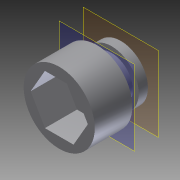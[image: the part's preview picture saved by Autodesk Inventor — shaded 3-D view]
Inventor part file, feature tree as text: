
AUTODESK INVENTOR PART (.ipt)
format: ipt  version: 2012 (Build 160160000, 160)  size: 111,104 bytes
history: native  units: in
note: dims shown in document units (in); Inventor stores cm internally (conversion verified against a paired STEP export)
features: extrude x4, sketch x4, plane x2
ambient origin geometry x8: Origin, YZ Plane, XZ Plane, XY Plane, X Axis, Y Axis, Z Axis, Center Point
bodies: Solid1 (feature_tree)
feature tree (10):
  plane  "Work Plane3"
  plane  "Work Plane4"
  extrude  "Extrusion5"  Depth=0.6264in
  extrude  "Extrusion6"  Depth=0.4921in
  extrude  "Extrusion7"  Depth=0.8183in
  extrude  "Extrusion8"  Depth=0.5709in
  sketch  "Sketch7"  dims[d17=0.2756in d18=0.6264in]
  sketch  "Sketch8"  dims[d19=0.1063in d20=0.0in d21=0.4921in]
  sketch  "Sketch9"  dims[d22=0.1063in d23=0.0in d24=0.8183in]
  sketch  "Sketch10"  dims[d25=0.4331in d26=0.0in d27=0.5709in d30=0.3701in d31=0.0in]
